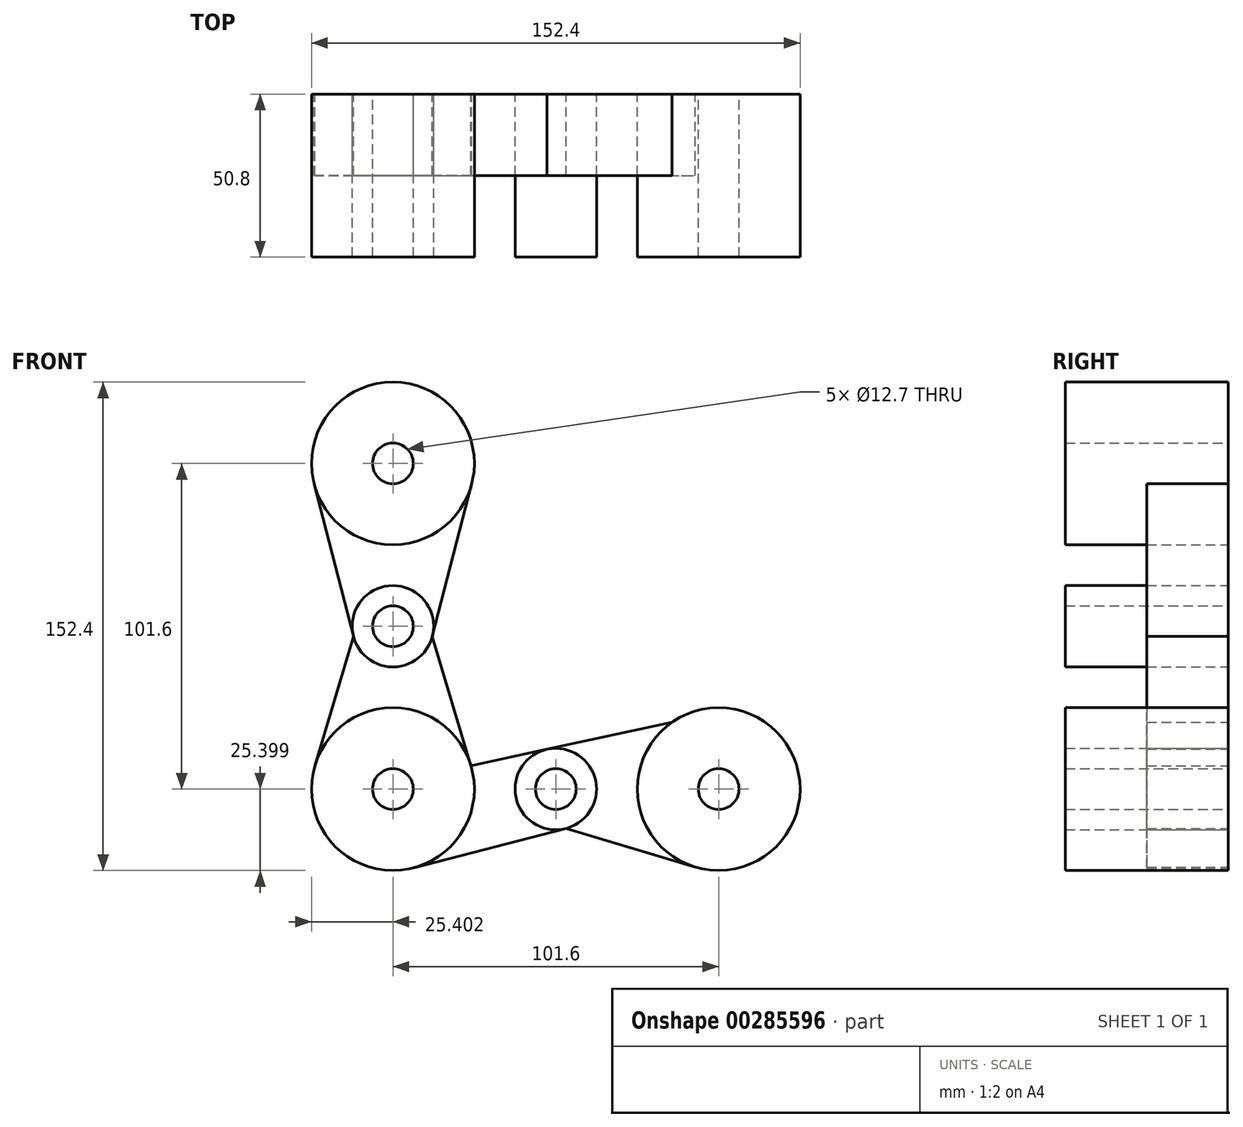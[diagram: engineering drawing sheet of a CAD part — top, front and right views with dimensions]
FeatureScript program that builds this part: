
annotation { "Feature Type Name" : "Feature", "Feature Type Description" : "" }
export const myFeature = defineFeature(function(context is Context, id is Id, definition is map)
    precondition{}
    {
        {
            var Q0;
            Q0=qCreatedBy(makeId("Front.planeOp"),FACE);
            var sketch = newSketch(context, id + "F0", { "sketchPlane" : qUnion([Q0])});
            skLineSegment(sketch, "E0", {"start": v(-140.1, -67.37) * mm, "end": v(-89.3, -67.37) * mm});
            skLineSegment(sketch, "E1", {"start": v(-89.3, -67.37) * mm, "end": v(-38.5, -67.37) * mm});
            skLineSegment(sketch, "E2", {"start": v(-140.1, -67.37) * mm, "end": v(-140.1, -16.57) * mm});
            skLineSegment(sketch, "E3", {"start": v(-140.1, 34.23) * mm, "end": v(-140.1, -16.57) * mm});
            skCircle(sketch, "E4", {"center": v(-140.1, 34.23) * mm, "radius": 25.4 * mm});
            skCircle(sketch, "E5", {"center": v(-140.1, -67.37) * mm, "radius": 25.4 * mm});
            skCircle(sketch, "E6", {"center": v(-38.5, -67.37) * mm, "radius": 25.4 * mm});
            skCircle(sketch, "E7", {"center": v(-140.1, -16.57) * mm, "radius": 12.7 * mm});
            skCircle(sketch, "E8", {"center": v(-89.3, -67.37) * mm, "radius": 12.7 * mm});
            skLineSegment(sketch, "E9", {"start": v(-164.7, 27.88) * mm, "end": v(-152.4, -19.75) * mm});
            skLineSegment(sketch, "E10", {"start": v(-152.4, -19.75) * mm, "end": v(-164.44, -60.1) * mm});
            skLineSegment(sketch, "E11", {"start": v(-115.5, 27.88) * mm, "end": v(-127.8, -19.75) * mm});
            skLineSegment(sketch, "E12", {"start": v(-127.8, -19.75) * mm, "end": v(-115.76, -60.1) * mm});
            skLineSegment(sketch, "E13", {"start": v(-133.75, -91.96) * mm, "end": v(-86.12, -79.67) * mm});
            skLineSegment(sketch, "E14", {"start": v(-86.12, -79.67) * mm, "end": v(-45.76, -91.71) * mm});
            skLineSegment(sketch, "E15", {"start": v(-115.76, -60.1) * mm, "end": v(-91.99, -54.96) * mm});
            skLineSegment(sketch, "E16", {"start": v(-91.99, -54.96) * mm, "end": v(-52.99, -46.51) * mm});
            skSolve(sketch);
        }
        {
            var Q0;
            {var subQ0=sQuery(id+"F0.wireOp",EDGE,"E4");var subQ1=makeQuery(id+"F0.imprint","INTERSECT",VERTEX,{"derivedFrom":[subQ0,sQuery(id+"F0.wireOp",EDGE,"E9")]});Q0=makeQuery(id+"F0.imprint","IMPRINT",FACE,{"disambiguationData":[TD([[makeQuery(id+"F0.imprint","IMPRINT",EDGE,{"disambiguationData":[TD([[subQ1,-1.0]])],"derivedFrom":subQ0}),1.0]])]});}
            var Q1;
            {var subQ0=sQuery(id+"F0.wireOp",EDGE,"E3");var subQ1=sQuery(id+"F0.wireOp",EDGE,"E2");var subQ2=makeQuery(id+"F0.imprint","INTERSECT",VERTEX,{"derivedFrom":[subQ1,subQ0]});Q1=makeQuery(id+"F0.imprint","IMPRINT",FACE,{"disambiguationData":[TD([[makeQuery(id+"F0.imprint","IMPRINT",EDGE,{"disambiguationData":[TD([[subQ2,1.0]])],"derivedFrom":subQ1}),-1.0]])]});}
            var Q2;
            {var subQ0=sQuery(id+"F0.wireOp",EDGE,"E3");var subQ1=sQuery(id+"F0.wireOp",EDGE,"E2");var subQ2=makeQuery(id+"F0.imprint","INTERSECT",VERTEX,{"derivedFrom":[subQ1,subQ0]});Q2=makeQuery(id+"F0.imprint","IMPRINT",FACE,{"disambiguationData":[TD([[makeQuery(id+"F0.imprint","IMPRINT",EDGE,{"disambiguationData":[TD([[subQ2,1.0]])],"derivedFrom":subQ1}),1.0]])]});}
            var Q3;
            {var subQ3=sQuery(id+"F0.wireOp",EDGE,"E2");var subQ4=sQuery(id+"F0.wireOp",EDGE,"E0");var subQ5=makeQuery(id+"F0.imprint","INTERSECT",VERTEX,{"derivedFrom":[subQ4,subQ3]});Q3=makeQuery(id+"F0.imprint","IMPRINT",FACE,{"disambiguationData":[TD([[makeQuery(id+"F0.imprint","IMPRINT",EDGE,{"disambiguationData":[TD([[subQ5,-1.0]])],"derivedFrom":subQ4}),-1.0]])]});}
            var Q4;
            {var subQ0=sQuery(id+"F0.wireOp",EDGE,"E2");var subQ1=sQuery(id+"F0.wireOp",EDGE,"E0");var subQ2=makeQuery(id+"F0.imprint","INTERSECT",VERTEX,{"derivedFrom":[subQ1,subQ0]});Q4=makeQuery(id+"F0.imprint","IMPRINT",FACE,{"disambiguationData":[TD([[makeQuery(id+"F0.imprint","IMPRINT",EDGE,{"disambiguationData":[TD([[subQ2,-1.0]])],"derivedFrom":subQ1}),1.0]])]});}
            var Q5;
            {var subQ0=sQuery(id+"F0.wireOp",EDGE,"E1");var subQ1=sQuery(id+"F0.wireOp",EDGE,"E0");var subQ2=makeQuery(id+"F0.imprint","INTERSECT",VERTEX,{"derivedFrom":[subQ1,subQ0]});Q5=makeQuery(id+"F0.imprint","IMPRINT",FACE,{"disambiguationData":[TD([[makeQuery(id+"F0.imprint","IMPRINT",EDGE,{"disambiguationData":[TD([[subQ2,1.0]])],"derivedFrom":subQ1}),1.0]])]});}
            var Q6;
            {var subQ0=sQuery(id+"F0.wireOp",EDGE,"E1");var subQ1=sQuery(id+"F0.wireOp",EDGE,"E0");var subQ2=makeQuery(id+"F0.imprint","INTERSECT",VERTEX,{"derivedFrom":[subQ1,subQ0]});Q6=makeQuery(id+"F0.imprint","IMPRINT",FACE,{"disambiguationData":[TD([[makeQuery(id+"F0.imprint","IMPRINT",EDGE,{"disambiguationData":[TD([[subQ2,1.0]])],"derivedFrom":subQ1}),-1.0]])]});}
            var Q7;
            {var subQ0=sQuery(id+"F0.wireOp",EDGE,"E6");var subQ1=makeQuery(id+"F0.imprint","INTERSECT",VERTEX,{"derivedFrom":[subQ0,sQuery(id+"F0.wireOp",EDGE,"E16")]});Q7=makeQuery(id+"F0.imprint","IMPRINT",FACE,{"disambiguationData":[TD([[makeQuery(id+"F0.imprint","IMPRINT",EDGE,{"disambiguationData":[TD([[subQ1,-1.0]])],"derivedFrom":subQ0}),1.0]])]});}
            extrude(context, id + "F1", {"entities" : qUnion([Q0, Q1, Q2, Q3, Q4, Q5, Q6, Q7]), "depth" : 50.8 * mm});
        }
        {
            var Q0;
            {var subQ5=sQuery(id+"F0.wireOp",EDGE,"E9");Q0=makeQuery(id+"F0.imprint","IMPRINT",FACE,{"disambiguationData":[TD([[makeQuery(id+"F0.imprint","IMPRINT",EDGE,{"derivedFrom":subQ5}),1.0]])]});}
            var Q1;
            {var subQ5=sQuery(id+"F0.wireOp",EDGE,"E11");Q1=makeQuery(id+"F0.imprint","IMPRINT",FACE,{"disambiguationData":[TD([[makeQuery(id+"F0.imprint","IMPRINT",EDGE,{"derivedFrom":subQ5}),-1.0]])]});}
            var Q2;
            {var subQ5=sQuery(id+"F0.wireOp",EDGE,"E12");Q2=makeQuery(id+"F0.imprint","IMPRINT",FACE,{"disambiguationData":[TD([[makeQuery(id+"F0.imprint","IMPRINT",EDGE,{"derivedFrom":subQ5}),-1.0]])]});}
            var Q3;
            {var subQ5=sQuery(id+"F0.wireOp",EDGE,"E10");Q3=makeQuery(id+"F0.imprint","IMPRINT",FACE,{"disambiguationData":[TD([[makeQuery(id+"F0.imprint","IMPRINT",EDGE,{"derivedFrom":subQ5}),1.0]])]});}
            var Q4;
            {var subQ5=sQuery(id+"F0.wireOp",EDGE,"E16");Q4=makeQuery(id+"F0.imprint","IMPRINT",FACE,{"disambiguationData":[TD([[makeQuery(id+"F0.imprint","IMPRINT",EDGE,{"derivedFrom":subQ5}),-1.0]])]});}
            var Q5;
            {var subQ5=sQuery(id+"F0.wireOp",EDGE,"E14");Q5=makeQuery(id+"F0.imprint","IMPRINT",FACE,{"disambiguationData":[TD([[makeQuery(id+"F0.imprint","IMPRINT",EDGE,{"derivedFrom":subQ5}),1.0]])]});}
            var Q6;
            {var subQ5=sQuery(id+"F0.wireOp",EDGE,"E13");Q6=makeQuery(id+"F0.imprint","IMPRINT",FACE,{"disambiguationData":[TD([[makeQuery(id+"F0.imprint","IMPRINT",EDGE,{"derivedFrom":subQ5}),1.0]])]});}
            var Q7;
            {var subQ5=sQuery(id+"F0.wireOp",EDGE,"E15");Q7=makeQuery(id+"F0.imprint","IMPRINT",FACE,{"disambiguationData":[TD([[makeQuery(id+"F0.imprint","IMPRINT",EDGE,{"derivedFrom":subQ5}),-1.0]])]});}
            extrude(context, id + "F2", {"entities" : qUnion([Q0, Q1, Q2, Q3, Q4, Q5, Q6, Q7]), "depth" : 25.4 * mm});
        }
        {
            var Q0;
            Q0=sQuery(id+"F0.wireOp",VERTEX,"E4.center");
            var Q1;
            Q1=sQuery(id+"F0.wireOp",VERTEX,"E7.center");
            var Q2;
            Q2=sQuery(id+"F0.wireOp",VERTEX,"E5.center");
            var Q3;
            Q3=sQuery(id+"F0.wireOp",VERTEX,"E8.center");
            var Q4;
            Q4=sQuery(id+"F0.wireOp",VERTEX,"E1.end");
            var Q5;
            Q5=makeQuery(id+"F1.opExtrude","SWEPT_BODY",BODY,{"disambiguationData":[OSD([sQuery(id+"F0.wireOp",EDGE,"E4")])]});
            var Q6;
            Q6=makeQuery(id+"F1.opExtrude","SWEPT_BODY",BODY,{"disambiguationData":[OSD([sQuery(id+"F0.wireOp",EDGE,"E7")])]});
            var Q7;
            Q7=makeQuery(id+"F1.opExtrude","SWEPT_BODY",BODY,{"disambiguationData":[OSD([sQuery(id+"F0.wireOp",EDGE,"E5")])]});
            var Q8;
            Q8=makeQuery(id+"F1.opExtrude","SWEPT_BODY",BODY,{"disambiguationData":[OSD([sQuery(id+"F0.wireOp",EDGE,"E8")])]});
            var Q9;
            Q9=makeQuery(id+"F1.opExtrude","SWEPT_BODY",BODY,{"disambiguationData":[OSD([sQuery(id+"F0.wireOp",EDGE,"E6")])]});
            hole(context, id + "F3", {"style" : HoleStyle.SIMPLE, "endStyle" : HoleEndStyle.THROUGH, "oppositeDirection" : true, "holeDiameter" : 12.7 * mm, "tappedDepth" : 12.7 * mm, "tapClearance" : 3, "locations" : qUnion([Q0, Q1, Q2, Q3, Q4]), "scope" : qUnion([Q5, Q6, Q7, Q8, Q9])});
        }
    });
